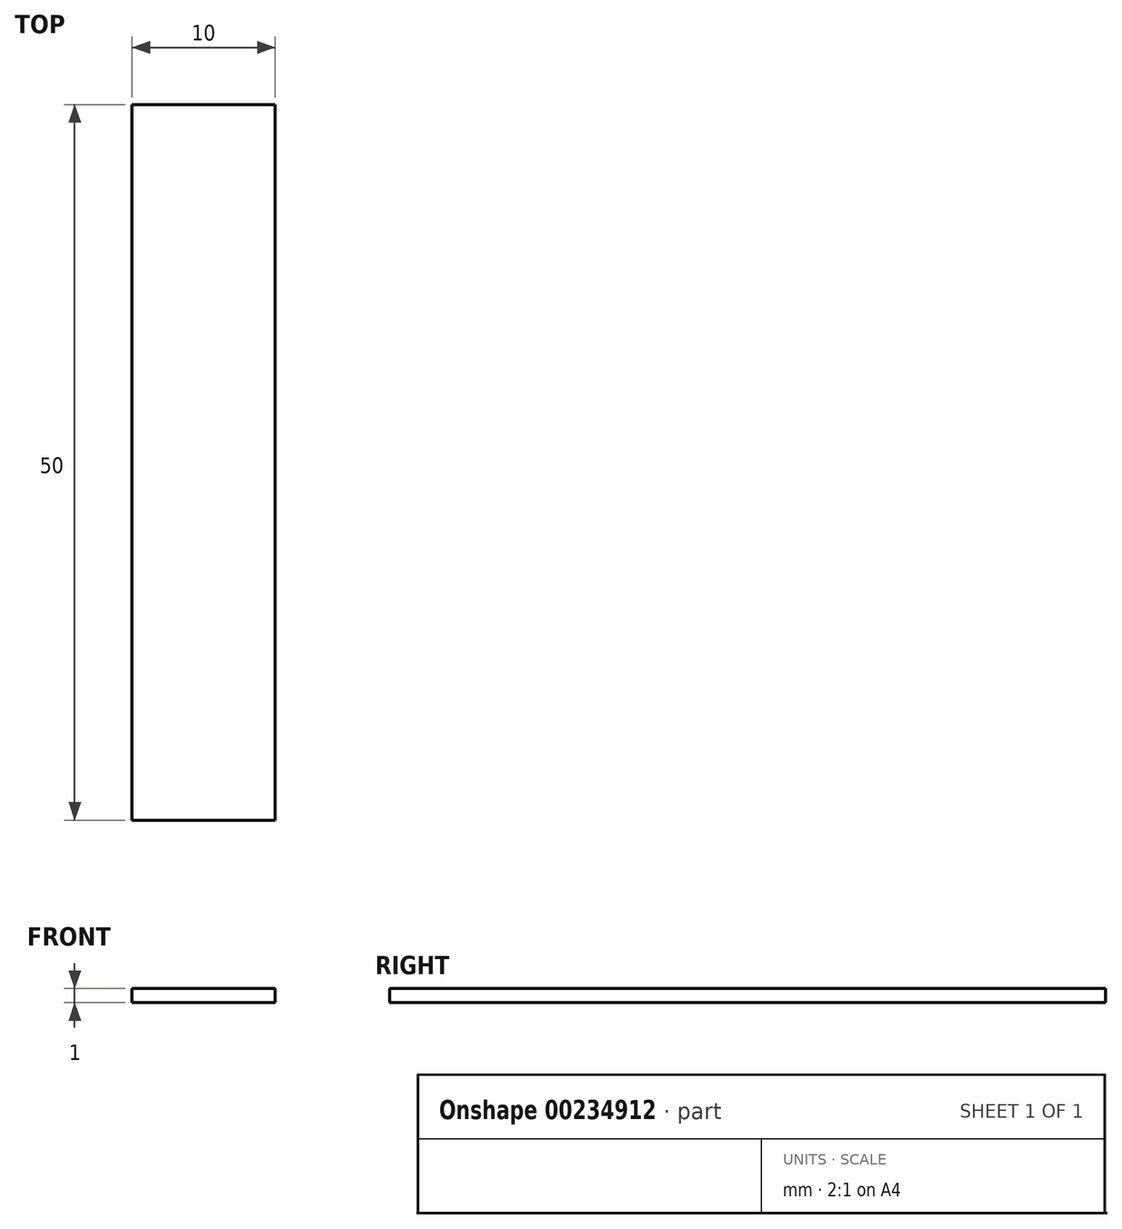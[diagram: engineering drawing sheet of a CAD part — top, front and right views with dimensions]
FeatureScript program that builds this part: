
annotation { "Feature Type Name" : "Feature", "Feature Type Description" : "" }
export const myFeature = defineFeature(function(context is Context, id is Id, definition is map)
    precondition{}
    {
        {
            var Q0;
            Q0=qCreatedBy(makeId("Top.planeOp"),FACE);
            var sketch = newSketch(context, id + "F0", { "sketchPlane" : qUnion([Q0])});
            skLineSegment(sketch, "E0.bottom", {"start": v(5, 25) * mm, "end": v(-5, 25) * mm});
            skLineSegment(sketch, "E0.top", {"start": v(5, -25) * mm, "end": v(-5, -25) * mm});
            skLineSegment(sketch, "E0.left", {"start": v(5, 25) * mm, "end": v(5, -25) * mm});
            skLineSegment(sketch, "E0.right", {"start": v(-5, 25) * mm, "end": v(-5, -25) * mm});
            skPoint(sketch, "E0.middle", {"position": v(0, 0) * mm});
            skSolve(sketch);
        }
        {
            var Q0;
            Q0 = qSketchRegion(id + "F0", true);
            extrude(context, id + "F1", {"entities" : qUnion([Q0]), "depth" : 1 * mm});
        }
    });
